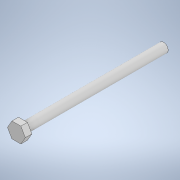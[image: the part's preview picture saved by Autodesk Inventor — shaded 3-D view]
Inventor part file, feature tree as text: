
AUTODESK INVENTOR PART (.ipt)
format: ipt  version: 2022 (Build 260153000, 153)  size: 109,568 bytes
history: native  units: mm
features: extrude x2, sketch x2
ambient origin geometry x8: Origin, YZ Plane, XZ Plane, XY Plane, X Axis, Y Axis, Z Axis, Center Point
bodies: Solid1 (feature_tree)
feature tree (4):
  extrude  "Extrusion1"  Depth=3.9mm TaperAngle=360.0deg
  extrude  "Extrusion2"  Depth=61.3mm
  sketch  "Sketch1"  dims[d0=3.9mm d1=60.0mm d3=360.0deg]
  sketch  "Sketch2"  dims[d5=2.85mm d6=0.0mm d7=4.0mm d8=61.3mm d9=0.0mm d10=0.5mm d11=0.872665mm d12=0.5mm d13=0.872665mm]
